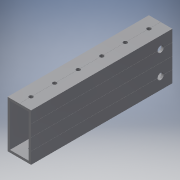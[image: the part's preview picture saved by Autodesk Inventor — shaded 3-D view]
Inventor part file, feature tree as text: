
AUTODESK INVENTOR PART (.ipt)
format: ipt  version: 2017 (Build 210142000, 142)  size: 471,552 bytes
history: native  units: in
note: dims shown in document units (in); Inventor stores cm internally (conversion verified against a paired STEP export)
features: hole x2, extrude x1, sketch x1, other x1
ambient origin geometry x8: Origin, YZ Plane, XZ Plane, XY Plane, X Axis, Y Axis, Z Axis, Center Point
bodies: Solid1 (feature_tree)
feature tree (5):
  extrude  "Extrusion2"  Depth=1.0in TaperAngle=0.0deg
  hole  "Hole1"  [1 undecoded]
  hole  "Hole2"  [1 undecoded]
  sketch  "Sketch1"  dims[d0=6.0in d3=1.0in d4=0.0in d5=0.5in d6=0.5in d7=0.2656in d8=0.75in d9=0.375in d10=0.25in d11=0.5635in d12=1.0in d13=0.8108in d14=0.5in d15=0.5in d16=0.2656in d17=0.75in d18=0.375in d19=0.25in d20=0.5635in d21=1.0in d22=0.8108in]
  other  "Cut-Extrude2"
note: 2 required parameter values undecoded (feature->parameter linkage not recoverable at this tier; creation-order binding heuristic only, values carry confidence <= 0.55)
